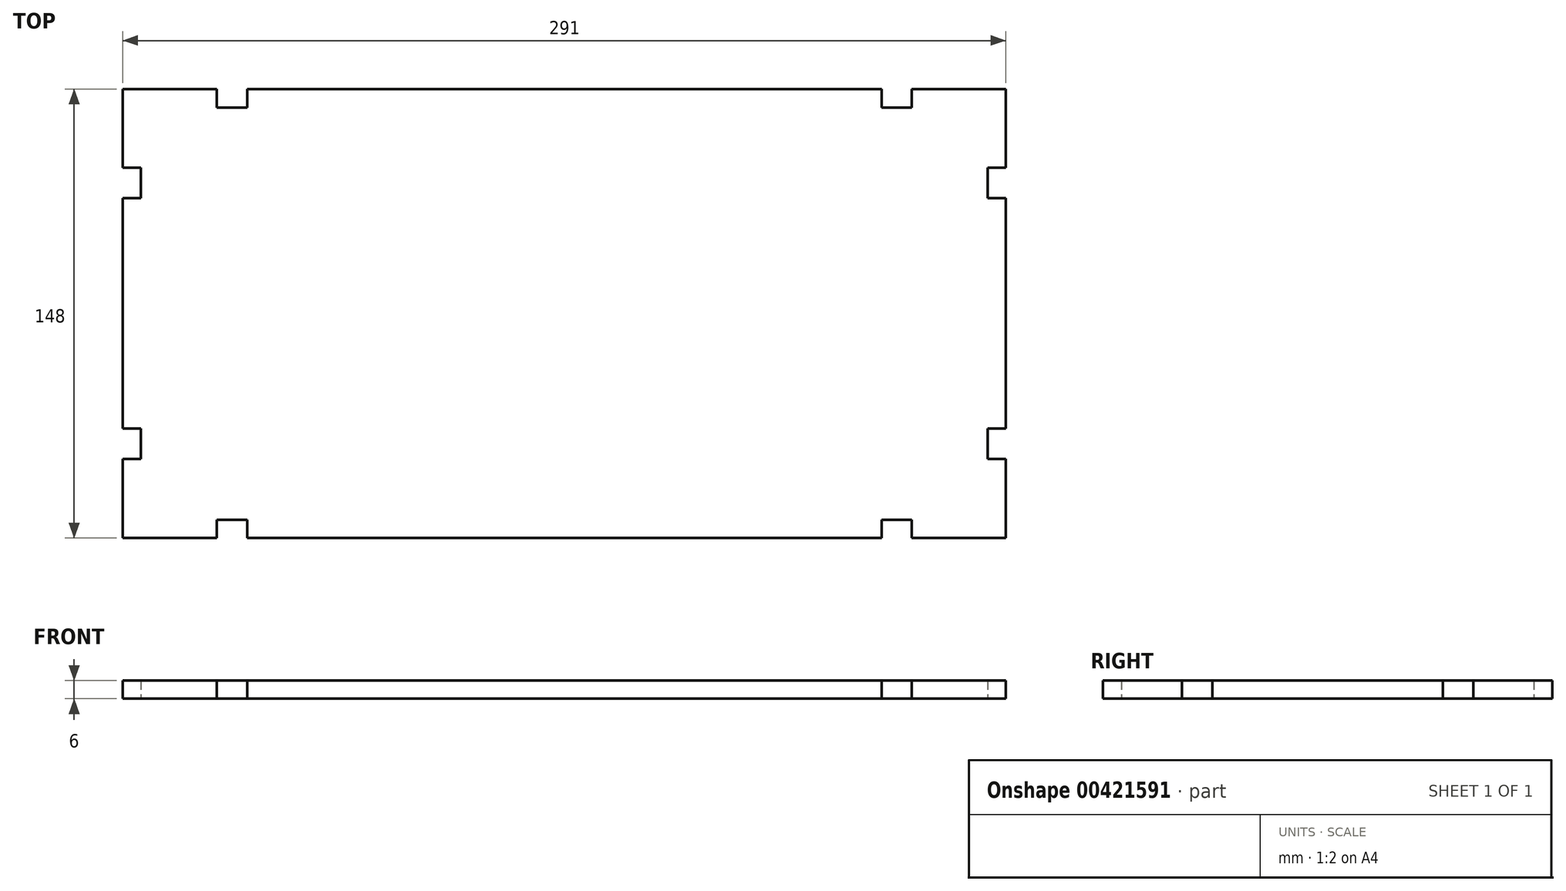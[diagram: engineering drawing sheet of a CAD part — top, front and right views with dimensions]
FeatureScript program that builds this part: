
annotation { "Feature Type Name" : "Feature", "Feature Type Description" : "" }
export const myFeature = defineFeature(function(context is Context, id is Id, definition is map)
    precondition{}
    {
        {
            var Q0;
            Q0=qCreatedBy(makeId("Top.planeOp"),FACE);
            var sketch = newSketch(context, id + "F0", { "sketchPlane" : qUnion([Q0])});
            skLineSegment(sketch, "E0.bottom", {"start": v(-145.5, 43.51) * mm, "end": v(-139.5, 43.51) * mm});
            skLineSegment(sketch, "E0.top", {"start": v(-145.5, 33.51) * mm, "end": v(-139.5, 33.51) * mm});
            skLineSegment(sketch, "E1.bottom", {"start": v(-145.5, -42.49) * mm, "end": v(-139.5, -42.49) * mm});
            skLineSegment(sketch, "E1.top", {"start": v(-145.5, -52.49) * mm, "end": v(-139.5, -52.49) * mm});
            skLineSegment(sketch, "E2", {"start": v(-145.5, -78.49) * mm, "end": v(-114.5, -78.5) * mm});
            skLineSegment(sketch, "E3.left", {"start": v(-114.5, -78.5) * mm, "end": v(-114.5, -72.5) * mm});
            skLineSegment(sketch, "E3.right", {"start": v(-104.5, -78.5) * mm, "end": v(-104.5, -72.5) * mm});
            skLineSegment(sketch, "E4.MirrorCS", {"start": v(-104.5, 69.4) * mm, "end": v(-104.5, 63.4) * mm});
            skLineSegment(sketch, "E5", {"start": v(-114.5, 69.4) * mm, "end": v(-145.5, 69.51) * mm});
            skLineSegment(sketch, "E6", {"start": v(-145.5, 33.51) * mm, "end": v(-145.5, -42.49) * mm});
            skLineSegment(sketch, "E7", {"start": v(-104.5, -78.5) * mm, "end": v(0, -78.5) * mm});
            skLineSegment(sketch, "E8", {"start": v(-104.5, 69.4) * mm, "end": v(0, 69.4) * mm});
            skLineSegment(sketch, "E9", {"start": v(-145.5, -52.49) * mm, "end": v(-145.5, -78.49) * mm});
            skLineSegment(sketch, "E10", {"start": v(-145.5, 43.51) * mm, "end": v(-145.5, 69.51) * mm});
            skLineSegment(sketch, "E11", {"start": v(-114.5, 69.4) * mm, "end": v(-114.5, 63.4) * mm});
            skLineSegment(sketch, "E12.MirrorCS", {"start": v(104.5, -78.5) * mm, "end": v(104.5, -72.5) * mm});
            skLineSegment(sketch, "E13.MirrorCS", {"start": v(145.5, -52.49) * mm, "end": v(139.5, -52.49) * mm});
            skLineSegment(sketch, "E14.MirrorCS", {"start": v(114.5, 69.4) * mm, "end": v(114.5, 63.4) * mm});
            skLineSegment(sketch, "E15.MirrorCS", {"start": v(114.5, -78.5) * mm, "end": v(114.5, -72.5) * mm});
            skLineSegment(sketch, "E16.MirrorCS", {"start": v(104.5, 69.4) * mm, "end": v(104.5, 63.4) * mm});
            skLineSegment(sketch, "E17.MirrorCS", {"start": v(145.5, 43.51) * mm, "end": v(139.5, 43.51) * mm});
            skLineSegment(sketch, "E18.MirrorCS", {"start": v(145.5, 33.51) * mm, "end": v(139.5, 33.51) * mm});
            skLineSegment(sketch, "E19.MirrorCS", {"start": v(145.5, -42.49) * mm, "end": v(139.5, -42.49) * mm});
            skLineSegment(sketch, "E20.MirrorCS", {"start": v(114.5, -72.5) * mm, "end": v(104.5, -72.5) * mm});
            skLineSegment(sketch, "E21.MirrorCS", {"start": v(139.5, -42.49) * mm, "end": v(139.5, -52.49) * mm});
            skLineSegment(sketch, "E22.MirrorCS", {"start": v(139.5, 33.51) * mm, "end": v(139.5, 43.51) * mm});
            skLineSegment(sketch, "E23.MirrorCS", {"start": v(114.5, 63.4) * mm, "end": v(104.5, 63.4) * mm});
            skLineSegment(sketch, "E24.MirrorCS", {"start": v(114.5, 69.4) * mm, "end": v(145.5, 69.51) * mm});
            skLineSegment(sketch, "E25.MirrorCS", {"start": v(145.5, 33.51) * mm, "end": v(145.5, -42.49) * mm});
            skLineSegment(sketch, "E26.MirrorCS", {"start": v(145.5, 43.51) * mm, "end": v(145.5, 69.51) * mm});
            skLineSegment(sketch, "E27.MirrorCS", {"start": v(145.5, -52.49) * mm, "end": v(145.5, -78.49) * mm});
            skLineSegment(sketch, "E28.MirrorCS", {"start": v(104.5, 69.4) * mm, "end": v(0, 69.4) * mm});
            skLineSegment(sketch, "E29.MirrorCS", {"start": v(104.5, -78.5) * mm, "end": v(0, -78.5) * mm});
            skLineSegment(sketch, "E30.MirrorCS", {"start": v(145.5, -78.49) * mm, "end": v(114.5, -78.5) * mm});
            skLineSegment(sketch, "E31", {"start": v(-114.5, 63.4) * mm, "end": v(-104.5, 63.4) * mm});
            skLineSegment(sketch, "E32", {"start": v(-139.5, 43.51) * mm, "end": v(-139.5, 33.51) * mm});
            skLineSegment(sketch, "E33", {"start": v(-139.5, -42.49) * mm, "end": v(-139.5, -52.49) * mm});
            skLineSegment(sketch, "E34", {"start": v(-114.5, -72.5) * mm, "end": v(-104.5, -72.5) * mm});
            skSolve(sketch);
        }
        {
            var Q0;
            Q0=makeQuery(id+"F0.imprint","IMPRINT",FACE,{"disambiguationData":[TD([[makeQuery(id+"F0.imprint","IMPRINT",EDGE,{"derivedFrom":sQuery(id+"F0.wireOp",EDGE,"f668ead6-43b8-45e4-8231-2b9a8cdf18a7.left")}),1.0]])]});
            var Q1;
            Q1=makeQuery(id+"F0.imprint","IMPRINT",FACE,{"disambiguationData":[TD([[makeQuery(id+"F0.imprint","IMPRINT",EDGE,{"derivedFrom":sQuery(id+"F0.wireOp",EDGE,"E0.bottom")}),1.0]])]});
            extrude(context, id + "F1", {"entities" : qUnion([Q0, Q1]), "depth" : 6 * mm, "offsetDistance" : 25 * mm});
        }
    });
